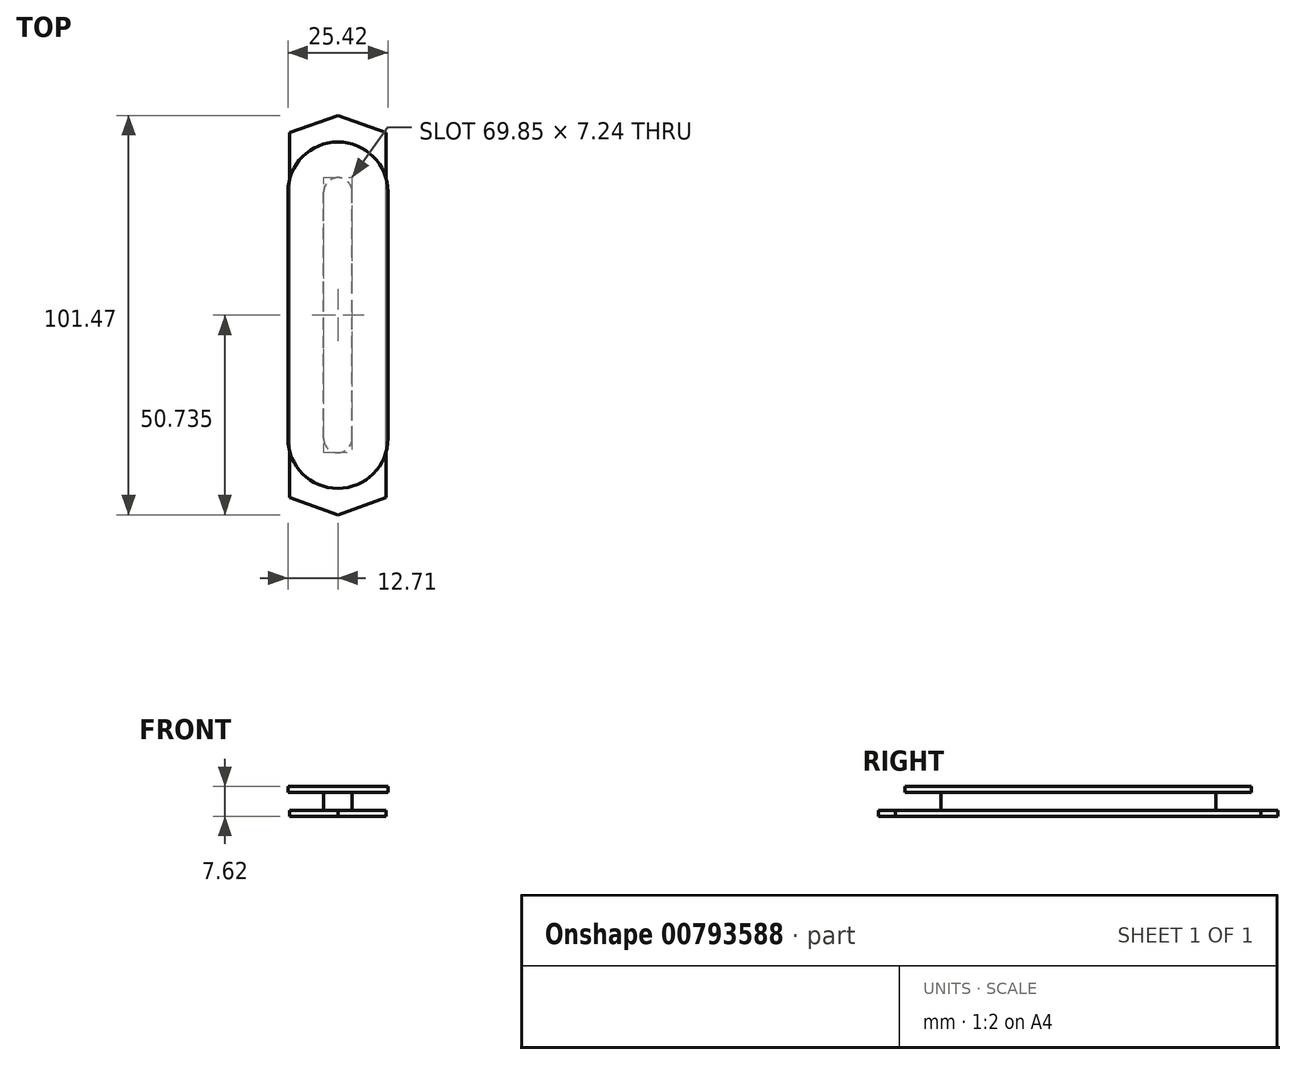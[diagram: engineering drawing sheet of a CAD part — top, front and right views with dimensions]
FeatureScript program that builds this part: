
annotation { "Feature Type Name" : "Feature", "Feature Type Description" : "" }
export const myFeature = defineFeature(function(context is Context, id is Id, definition is map)
    precondition{}
    {
        {
            var Q0;
            Q0=qCreatedBy(makeId("Top.planeOp"),FACE);
            var sketch = newSketch(context, id + "F0", { "sketchPlane" : qUnion([Q0])});
            skLineSegment(sketch, "E0.bottom", {"start": v(-3.62, 0) * mm, "end": v(-3.62, 0) * mm});
            skLineSegment(sketch, "E0.top", {"start": v(-3.62, 69.85) * mm, "end": v(-3.62, 69.85) * mm});
            skLineSegment(sketch, "E0.left", {"start": v(0, 3.62) * mm, "end": v(0, 66.23) * mm});
            skLineSegment(sketch, "E0.right", {"start": v(-7.24, 3.62) * mm, "end": v(-7.24, 66.23) * mm});
            skPoint(sketch, "E1.visualSharp", {"position": v(0, 0) * mm});
            skArc(sketch, "E1.filletArc", {"start": v(-3.62, 0) * mm, "mid": v(-1.06, 1.06) * mm, "end": v(0, 3.62) * mm});
            skPoint(sketch, "E2.visualSharp", {"position": v(-7.24, 0) * mm});
            skArc(sketch, "E2.filletArc", {"start": v(-7.24, 3.62) * mm, "mid": v(-6.18, 1.06) * mm, "end": v(-3.62, 0) * mm});
            skPoint(sketch, "E3.visualSharp", {"position": v(0, 69.85) * mm});
            skArc(sketch, "E3.filletArc", {"start": v(0, 66.23) * mm, "mid": v(-1.06, 68.79) * mm, "end": v(-3.62, 69.85) * mm});
            skPoint(sketch, "E4.visualSharp", {"position": v(-7.24, 69.85) * mm});
            skArc(sketch, "E4.filletArc", {"start": v(-3.62, 69.85) * mm, "mid": v(-6.18, 68.79) * mm, "end": v(-7.24, 66.23) * mm});
            skSolve(sketch);
        }
        {
            var Q0;
            Q0 = qSketchRegion(id + "F0", true);
            extrude(context, id + "F1", {"entities" : qUnion([Q0]), "depth" : 7.62 * mm, "offsetDistance" : 25.4 * mm});
        }
        {
            var Q0;
            Q0=makeQuery(id+"F1.opExtrude","CAP_FACE",FACE,{"disambiguationData":[OSD([sQuery(id+"F0.wireOp",EDGE,"E0.left"),sQuery(id+"F0.wireOp",EDGE,"E0.right"),sQuery(id+"F0.wireOp",EDGE,"E1.filletArc"),sQuery(id+"F0.wireOp",EDGE,"E2.filletArc"),sQuery(id+"F0.wireOp",EDGE,"E3.filletArc"),sQuery(id+"F0.wireOp",EDGE,"E4.filletArc")])],"isStart":true});
            var sketch = newSketch(context, id + "F2", { "sketchPlane" : qUnion([Q0])});
            skLineSegment(sketch, "E5.0", {"start": v(-17.9, -3.62) * mm, "end": v(-17.9, -66.23) * mm});
            skLineSegment(sketch, "E5.2", {"start": v(10.67, -66.23) * mm, "end": v(10.67, -3.62) * mm});
            skLineSegment(sketch, "E6.left", {"start": v(10.67, -3.62) * mm, "end": v(10.67, 12.9) * mm});
            skLineSegment(sketch, "E6.right", {"start": v(-17.9, -3.62) * mm, "end": v(-17.9, 12.9) * mm});
            skLineSegment(sketch, "E7", {"start": v(-3.62, 17.97) * mm, "end": v(10.67, 12.9) * mm});
            skLineSegment(sketch, "E8", {"start": v(-3.62, 17.97) * mm, "end": v(-17.9, 12.9) * mm});
            skLineSegment(sketch, "E9.left", {"start": v(10.67, -66.23) * mm, "end": v(10.67, -82.74) * mm});
            skLineSegment(sketch, "E9.right", {"start": v(-17.9, -66.23) * mm, "end": v(-17.9, -82.74) * mm});
            skLineSegment(sketch, "E10", {"start": v(-3.62, -87.82) * mm, "end": v(10.67, -82.74) * mm});
            skLineSegment(sketch, "E11", {"start": v(-3.62, -87.82) * mm, "end": v(-17.9, -82.74) * mm});
            skPoint(sketch, "E12.orphan", {"position": v(10.67, 17.97) * mm});
            skPoint(sketch, "E13.orphan", {"position": v(-17.9, 17.97) * mm});
            skPoint(sketch, "E14.orphan", {"position": v(10.67, -87.82) * mm});
            skPoint(sketch, "E15.orphan", {"position": v(-17.9, -87.82) * mm});
            skLineSegment(sketch, "E16.0", {"start": v(-3.62, 15.81) * mm, "end": v(8.64, 11.46) * mm});
            skLineSegment(sketch, "E17.0", {"start": v(-3.62, 15.81) * mm, "end": v(-15.88, 11.46) * mm});
            skLineSegment(sketch, "E18.1", {"start": v(-15.88, -3.62) * mm, "end": v(-15.88, -66.23) * mm});
            skLineSegment(sketch, "E18.2", {"start": v(-15.88, -66.23) * mm, "end": v(-15.88, -81.3) * mm});
            skLineSegment(sketch, "E19.1", {"start": v(8.64, -66.23) * mm, "end": v(8.64, -3.62) * mm});
            skLineSegment(sketch, "E19.2", {"start": v(8.64, -66.23) * mm, "end": v(8.64, -81.3) * mm});
            skLineSegment(sketch, "E20.0", {"start": v(-3.62, -85.66) * mm, "end": v(8.64, -81.3) * mm});
            skLineSegment(sketch, "E20.1", {"start": v(-3.62, -85.66) * mm, "end": v(-15.88, -81.3) * mm});
            skLineSegment(sketch, "E21", {"start": v(8.64, -3.62) * mm, "end": v(8.64, 11.46) * mm});
            skLineSegment(sketch, "E22", {"start": v(-15.88, -3.62) * mm, "end": v(-15.88, 11.46) * mm});
            skSolve(sketch);
        }
        {
            var Q0;
            Q0=makeQuery(id+"F2.imprint","IMPRINT",FACE,{"disambiguationData":[TD([[makeQuery(id+"F2.imprint","IMPRINT",EDGE,{"derivedFrom":sQuery(id+"F2.wireOp",EDGE,"E16.0")}),-1.0]])]});
            extrude(context, id + "F3", {"entities" : qUnion([Q0]), "operationType" : NewBodyOperationType.ADD, "oppositeDirection" : true, "depth" : 1.57 * mm, "offsetDistance" : 25.4 * mm});
        }
        {
            var Q0;
            Q0=makeQuery(id+"F1.opExtrude","CAP_FACE",FACE,{"disambiguationData":[OSD([sQuery(id+"F0.wireOp",EDGE,"E0.left"),sQuery(id+"F0.wireOp",EDGE,"E0.right"),sQuery(id+"F0.wireOp",EDGE,"E1.filletArc"),sQuery(id+"F0.wireOp",EDGE,"E2.filletArc"),sQuery(id+"F0.wireOp",EDGE,"E3.filletArc"),sQuery(id+"F0.wireOp",EDGE,"E4.filletArc")])],"isStart":false});
            var sketch = newSketch(context, id + "F4", { "sketchPlane" : qUnion([Q0])});
            skLineSegment(sketch, "E23.0", {"start": v(-16.33, 66.23) * mm, "end": v(-16.33, 3.62) * mm});
            skArc(sketch, "E23.1", {"start": v(9.1, 66.23) * mm, "mid": v(-3.62, 78.94) * mm, "end": v(-16.33, 66.23) * mm});
            skLineSegment(sketch, "E23.2", {"start": v(9.1, 3.62) * mm, "end": v(9.1, 66.23) * mm});
            skArc(sketch, "E23.3", {"start": v(-16.33, 3.62) * mm, "mid": v(-3.62, -9.1) * mm, "end": v(9.1, 3.62) * mm});
            skSolve(sketch);
        }
        {
            var Q0;
            Q0=makeQuery(id+"F4.imprint","IMPRINT",FACE,{"disambiguationData":[TD([[makeQuery(id+"F4.imprint","IMPRINT",EDGE,{"derivedFrom":sQuery(id+"F4.wireOp",EDGE,"E23.0")}),1.0]])]});
            extrude(context, id + "F5", {"entities" : qUnion([Q0]), "operationType" : NewBodyOperationType.ADD, "oppositeDirection" : true, "depth" : 1.57 * mm, "offsetDistance" : 25.4 * mm});
        }
    });
